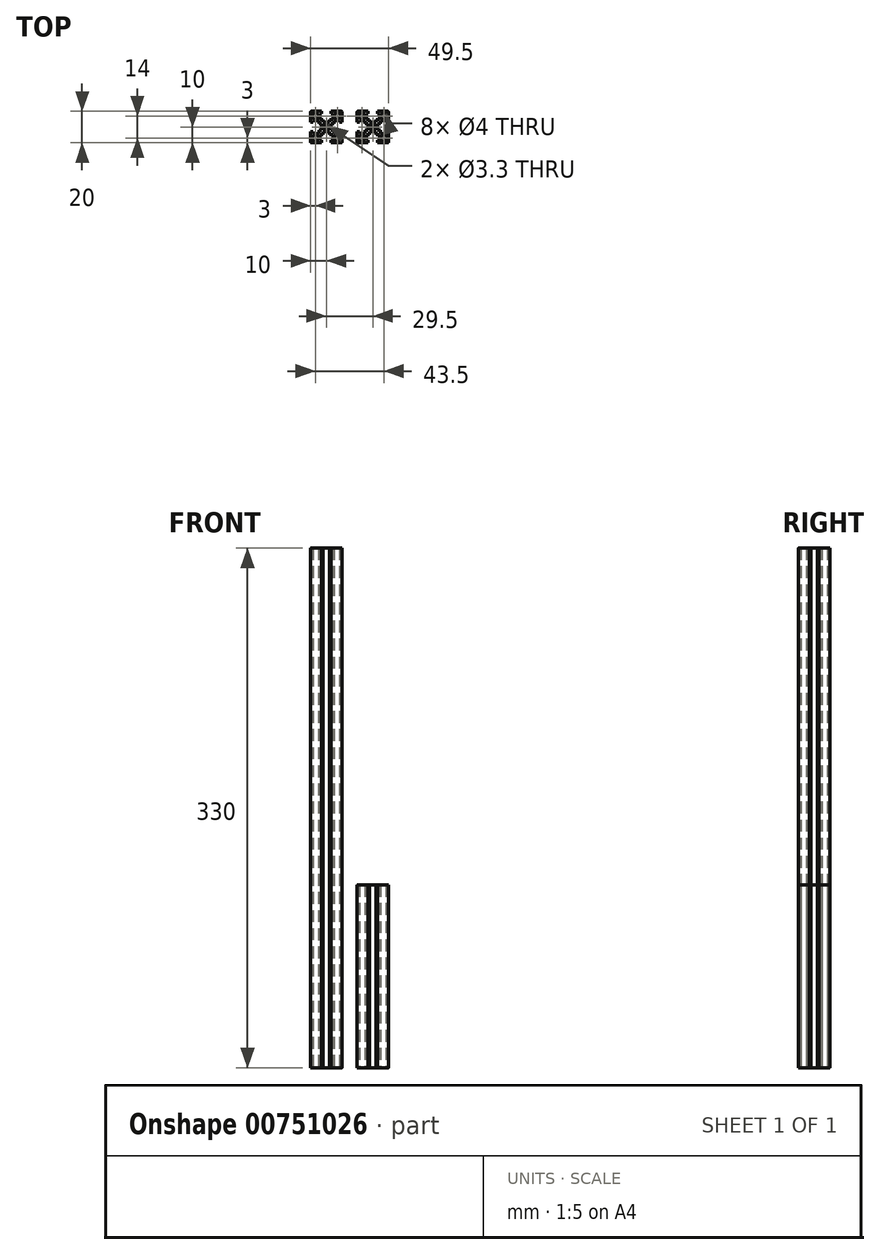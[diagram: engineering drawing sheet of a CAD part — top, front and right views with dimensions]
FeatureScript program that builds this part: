
annotation { "Feature Type Name" : "Feature", "Feature Type Description" : "" }
export const myFeature = defineFeature(function(context is Context, id is Id, definition is map)
    precondition{}
    {
        {
            var Q0;
            Q0=qCreatedBy(makeId("Top.planeOp"),FACE);
            var sketch = newSketch(context, id + "F0", { "sketchPlane" : qUnion([Q0])});
            skLineSegment(sketch, "E0", {"start": v(-9.48, 9.98) * mm, "end": v(-2.98, 9.98) * mm});
            skLineSegment(sketch, "E1", {"start": v(-2.98, 9.98) * mm, "end": v(-2.98, 8.48) * mm});
            skLineSegment(sketch, "E2", {"start": v(-2.98, 8.48) * mm, "end": v(-4.13, 8.48) * mm});
            skLineSegment(sketch, "E3", {"start": v(-4.13, 8.48) * mm, "end": v(-4.13, 4.78) * mm});
            skLineSegment(sketch, "E4", {"start": v(-4.13, 4.78) * mm, "end": v(-2.13, 4.78) * mm});
            skLineSegment(sketch, "E5", {"start": v(-2.13, 4.78) * mm, "end": v(-2.13, 2.98) * mm});
            skLineSegment(sketch, "E6", {"start": v(-2.13, 2.98) * mm, "end": v(0.02, 2.98) * mm});
            skLineSegment(sketch, "E7", {"start": v(0.02, 2.98) * mm, "end": v(0.02, -0.02) * mm});
            skLineSegment(sketch, "E8", {"start": v(0.02, -0.02) * mm, "end": v(-9.98, 9.98) * mm});
            skLineSegment(sketch, "E9.MirrorCS", {"start": v(-9.98, 9.48) * mm, "end": v(-9.98, 2.98) * mm});
            skLineSegment(sketch, "E10.MirrorCS", {"start": v(-8.48, 2.98) * mm, "end": v(-8.48, 4.13) * mm});
            skLineSegment(sketch, "E11.MirrorCS", {"start": v(-4.78, 2.13) * mm, "end": v(-2.98, 2.13) * mm});
            skLineSegment(sketch, "E12.MirrorCS", {"start": v(-9.98, 2.98) * mm, "end": v(-8.48, 2.98) * mm});
            skLineSegment(sketch, "E13.MirrorCS", {"start": v(-2.98, 2.13) * mm, "end": v(-2.98, -0.02) * mm});
            skLineSegment(sketch, "E14.MirrorCS", {"start": v(-4.78, 4.13) * mm, "end": v(-4.78, 2.13) * mm});
            skLineSegment(sketch, "E15.MirrorCS", {"start": v(-8.48, 4.13) * mm, "end": v(-4.78, 4.13) * mm});
            skLineSegment(sketch, "E16.MirrorCS", {"start": v(-2.98, -0.02) * mm, "end": v(0.02, -0.02) * mm});
            skCircle(sketch, "E17", {"center": v(-6.98, 6.98) * mm, "radius": 2 * mm});
            skLineSegment(sketch, "E18.1.0", {"start": v(-2.13, -3.02) * mm, "end": v(0.02, -3.02) * mm});
            skCircle(sketch, "E18.1.1", {"center": v(-6.98, -7.02) * mm, "radius": 2 * mm});
            skLineSegment(sketch, "E18.1.2", {"start": v(-2.98, -10.02) * mm, "end": v(-2.98, -8.52) * mm});
            skLineSegment(sketch, "E18.1.3", {"start": v(-2.13, -4.82) * mm, "end": v(-2.13, -3.02) * mm});
            skLineSegment(sketch, "E18.1.4", {"start": v(-2.98, -8.52) * mm, "end": v(-4.13, -8.52) * mm});
            skLineSegment(sketch, "E18.1.5", {"start": v(-9.48, -10.02) * mm, "end": v(-2.98, -10.02) * mm});
            skLineSegment(sketch, "E18.1.6", {"start": v(0.02, -0.02) * mm, "end": v(-9.98, -10.02) * mm});
            skLineSegment(sketch, "E18.1.7", {"start": v(-2.98, -2.17) * mm, "end": v(-2.98, -0.02) * mm});
            skLineSegment(sketch, "E18.1.8", {"start": v(-4.78, -2.17) * mm, "end": v(-2.98, -2.17) * mm});
            skLineSegment(sketch, "E18.1.9", {"start": v(-4.78, -4.17) * mm, "end": v(-4.78, -2.17) * mm});
            skLineSegment(sketch, "E18.1.10", {"start": v(-8.48, -4.17) * mm, "end": v(-4.78, -4.17) * mm});
            skLineSegment(sketch, "E18.1.11", {"start": v(-8.48, -3.02) * mm, "end": v(-8.48, -4.17) * mm});
            skLineSegment(sketch, "E18.1.12", {"start": v(-9.98, -3.02) * mm, "end": v(-8.48, -3.02) * mm});
            skLineSegment(sketch, "E18.1.13", {"start": v(-9.98, -9.52) * mm, "end": v(-9.98, -3.02) * mm});
            skLineSegment(sketch, "E18.1.14", {"start": v(-4.13, -8.52) * mm, "end": v(-4.13, -4.82) * mm});
            skLineSegment(sketch, "E18.1.15", {"start": v(-4.13, -4.82) * mm, "end": v(-2.13, -4.82) * mm});
            skLineSegment(sketch, "E18.2.0", {"start": v(3.02, -2.17) * mm, "end": v(3.02, -0.02) * mm});
            skCircle(sketch, "E18.2.1", {"center": v(7.02, -7.02) * mm, "radius": 2 * mm});
            skLineSegment(sketch, "E18.2.2", {"start": v(10.02, -3.02) * mm, "end": v(8.52, -3.02) * mm});
            skLineSegment(sketch, "E18.2.3", {"start": v(4.82, -2.17) * mm, "end": v(3.02, -2.17) * mm});
            skLineSegment(sketch, "E18.2.4", {"start": v(8.52, -3.02) * mm, "end": v(8.52, -4.17) * mm});
            skLineSegment(sketch, "E18.2.5", {"start": v(10.02, -9.52) * mm, "end": v(10.02, -3.02) * mm});
            skLineSegment(sketch, "E18.2.6", {"start": v(0.02, -0.02) * mm, "end": v(10.02, -10.02) * mm});
            skLineSegment(sketch, "E18.2.7", {"start": v(2.17, -3.02) * mm, "end": v(0.02, -3.02) * mm});
            skLineSegment(sketch, "E18.2.8", {"start": v(2.17, -4.82) * mm, "end": v(2.17, -3.02) * mm});
            skLineSegment(sketch, "E18.2.9", {"start": v(4.17, -4.82) * mm, "end": v(2.17, -4.82) * mm});
            skLineSegment(sketch, "E18.2.10", {"start": v(4.17, -8.52) * mm, "end": v(4.17, -4.82) * mm});
            skLineSegment(sketch, "E18.2.11", {"start": v(3.02, -8.52) * mm, "end": v(4.17, -8.52) * mm});
            skLineSegment(sketch, "E18.2.12", {"start": v(3.02, -10.02) * mm, "end": v(3.02, -8.52) * mm});
            skLineSegment(sketch, "E18.2.13", {"start": v(9.52, -10.02) * mm, "end": v(3.02, -10.02) * mm});
            skLineSegment(sketch, "E18.2.14", {"start": v(8.52, -4.17) * mm, "end": v(4.82, -4.17) * mm});
            skLineSegment(sketch, "E18.2.15", {"start": v(4.82, -4.17) * mm, "end": v(4.82, -2.17) * mm});
            skLineSegment(sketch, "E18.3.0", {"start": v(2.17, 2.98) * mm, "end": v(0.02, 2.98) * mm});
            skCircle(sketch, "E18.3.1", {"center": v(7.02, 6.98) * mm, "radius": 2 * mm});
            skLineSegment(sketch, "E18.3.2", {"start": v(3.02, 9.98) * mm, "end": v(3.02, 8.48) * mm});
            skLineSegment(sketch, "E18.3.3", {"start": v(2.17, 4.78) * mm, "end": v(2.17, 2.98) * mm});
            skLineSegment(sketch, "E18.3.4", {"start": v(3.02, 8.48) * mm, "end": v(4.17, 8.48) * mm});
            skLineSegment(sketch, "E18.3.5", {"start": v(9.52, 9.98) * mm, "end": v(3.02, 9.98) * mm});
            skLineSegment(sketch, "E18.3.6", {"start": v(0.02, -0.02) * mm, "end": v(10.02, 9.98) * mm});
            skLineSegment(sketch, "E18.3.7", {"start": v(3.02, 2.13) * mm, "end": v(3.02, -0.02) * mm});
            skLineSegment(sketch, "E18.3.8", {"start": v(4.82, 2.13) * mm, "end": v(3.02, 2.13) * mm});
            skLineSegment(sketch, "E18.3.9", {"start": v(4.82, 4.13) * mm, "end": v(4.82, 2.13) * mm});
            skLineSegment(sketch, "E18.3.10", {"start": v(8.52, 4.13) * mm, "end": v(4.82, 4.13) * mm});
            skLineSegment(sketch, "E18.3.11", {"start": v(8.52, 2.98) * mm, "end": v(8.52, 4.13) * mm});
            skLineSegment(sketch, "E18.3.12", {"start": v(10.02, 2.98) * mm, "end": v(8.52, 2.98) * mm});
            skLineSegment(sketch, "E18.3.13", {"start": v(10.02, 9.48) * mm, "end": v(10.02, 2.98) * mm});
            skLineSegment(sketch, "E18.3.14", {"start": v(4.17, 8.48) * mm, "end": v(4.17, 4.78) * mm});
            skLineSegment(sketch, "E18.3.15", {"start": v(4.17, 4.78) * mm, "end": v(2.17, 4.78) * mm});
            skPoint(sketch, "E18.center", {"position": v(0.02, -0.02) * mm});
            skCircle(sketch, "E19", {"center": v(0.02, -0.02) * mm, "radius": 1.65 * mm});
            skPoint(sketch, "E20.visualSharp", {"position": v(-9.98, 9.98) * mm});
            skArc(sketch, "E20.filletArc", {"start": v(-9.48, 9.98) * mm, "mid": v(-9.83, 9.83) * mm, "end": v(-9.98, 9.48) * mm});
            skPoint(sketch, "E21.visualSharp", {"position": v(10.02, 9.98) * mm});
            skArc(sketch, "E21.filletArc", {"start": v(10.02, 9.48) * mm, "mid": v(9.87, 9.83) * mm, "end": v(9.52, 9.98) * mm});
            skPoint(sketch, "E22.visualSharp", {"position": v(10.02, -10.02) * mm});
            skArc(sketch, "E22.filletArc", {"start": v(9.52, -10.02) * mm, "mid": v(9.87, -9.87) * mm, "end": v(10.02, -9.52) * mm});
            skPoint(sketch, "E23.visualSharp", {"position": v(-9.98, -10.02) * mm});
            skArc(sketch, "E23.filletArc", {"start": v(-9.98, -9.52) * mm, "mid": v(-9.83, -9.87) * mm, "end": v(-9.48, -10.02) * mm});
            skSolve(sketch);
        }
        {
            var Q0;
            {var subQ8=sQuery(id+"F0.wireOp",EDGE,"E0");Q0=makeQuery(id+"F0.imprint","IMPRINT",FACE,{"disambiguationData":[TD([[makeQuery(id+"F0.imprint","IMPRINT",EDGE,{"derivedFrom":subQ8}),-1.0]])]});}
            var Q1;
            {var subQ9=sQuery(id+"F0.wireOp",EDGE,"E18.3.0");Q1=makeQuery(id+"F0.imprint","IMPRINT",FACE,{"disambiguationData":[TD([[makeQuery(id+"F0.imprint","IMPRINT",EDGE,{"derivedFrom":subQ9}),1.0]])]});}
            var Q2;
            {var subQ0=sQuery(id+"F0.wireOp",EDGE,"E18.1.7");Q2=makeQuery(id+"F0.imprint","IMPRINT",FACE,{"disambiguationData":[TD([[makeQuery(id+"F0.imprint","IMPRINT",EDGE,{"derivedFrom":subQ0}),-1.0]])]});}
            var Q3;
            Q3=makeQuery(id+"F0.imprint","IMPRINT",FACE,{"disambiguationData":[TD([[makeQuery(id+"F0.imprint","IMPRINT",EDGE,{"derivedFrom":sQuery(id+"F0.wireOp",EDGE,"E18.2.0")}),1.0]])]});
            var Q4;
            {var subQ11=sQuery(id+"F0.wireOp",EDGE,"E9.MirrorCS");Q4=makeQuery(id+"F0.imprint","IMPRINT",FACE,{"disambiguationData":[TD([[makeQuery(id+"F0.imprint","IMPRINT",EDGE,{"derivedFrom":subQ11}),1.0]])]});}
            var Q5;
            Q5=makeQuery(id+"F0.imprint","IMPRINT",FACE,{"disambiguationData":[TD([[makeQuery(id+"F0.imprint","IMPRINT",EDGE,{"derivedFrom":sQuery(id+"F0.wireOp",EDGE,"E18.1.0")}),1.0]])]});
            extrude(context, id + "F1", {"entities" : qUnion([Q0, Q1, Q2, Q3, Q4, Q5]), "depth" : 330 * mm, "offsetDistance" : 25 * mm});
        }
        {
            var Q0;
            Q0=qCreatedBy(makeId("Top.planeOp"),FACE);
            var sketch = newSketch(context, id + "F2", { "sketchPlane" : qUnion([Q0])});
            skLineSegment(sketch, "E24", {"start": v(20.02, 9.98) * mm, "end": v(26.52, 9.98) * mm});
            skLineSegment(sketch, "E25", {"start": v(26.52, 9.98) * mm, "end": v(26.52, 8.48) * mm});
            skLineSegment(sketch, "E26", {"start": v(26.52, 8.48) * mm, "end": v(25.37, 8.48) * mm});
            skLineSegment(sketch, "E27", {"start": v(25.37, 8.48) * mm, "end": v(25.37, 4.78) * mm});
            skLineSegment(sketch, "E28", {"start": v(25.37, 4.78) * mm, "end": v(27.37, 4.78) * mm});
            skLineSegment(sketch, "E29", {"start": v(27.37, 4.78) * mm, "end": v(27.37, 2.98) * mm});
            skLineSegment(sketch, "E30", {"start": v(27.37, 2.98) * mm, "end": v(29.52, 2.98) * mm});
            skLineSegment(sketch, "E31", {"start": v(29.52, 2.98) * mm, "end": v(29.52, -0.02) * mm});
            skLineSegment(sketch, "E32", {"start": v(29.52, -0.02) * mm, "end": v(19.52, 9.98) * mm});
            skLineSegment(sketch, "E33.MirrorCS", {"start": v(19.52, 9.48) * mm, "end": v(19.52, 2.98) * mm});
            skLineSegment(sketch, "E34.MirrorCS", {"start": v(21.02, 2.98) * mm, "end": v(21.02, 4.13) * mm});
            skLineSegment(sketch, "E35.MirrorCS", {"start": v(24.72, 2.13) * mm, "end": v(26.52, 2.13) * mm});
            skLineSegment(sketch, "E36.MirrorCS", {"start": v(19.52, 2.98) * mm, "end": v(21.02, 2.98) * mm});
            skLineSegment(sketch, "E37.MirrorCS", {"start": v(26.52, 2.13) * mm, "end": v(26.52, -0.02) * mm});
            skLineSegment(sketch, "E38.MirrorCS", {"start": v(24.72, 4.13) * mm, "end": v(24.72, 2.13) * mm});
            skLineSegment(sketch, "E39.MirrorCS", {"start": v(21.02, 4.13) * mm, "end": v(24.72, 4.13) * mm});
            skLineSegment(sketch, "E40.MirrorCS", {"start": v(26.52, -0.02) * mm, "end": v(29.52, -0.02) * mm});
            skCircle(sketch, "E41", {"center": v(22.52, 6.98) * mm, "radius": 2 * mm});
            skLineSegment(sketch, "E42.1.0", {"start": v(27.37, -3.02) * mm, "end": v(29.52, -3.02) * mm});
            skCircle(sketch, "E42.1.1", {"center": v(22.52, -7.02) * mm, "radius": 2 * mm});
            skLineSegment(sketch, "E42.1.2", {"start": v(26.52, -10.02) * mm, "end": v(26.52, -8.52) * mm});
            skLineSegment(sketch, "E42.1.3", {"start": v(27.37, -4.82) * mm, "end": v(27.37, -3.02) * mm});
            skLineSegment(sketch, "E42.1.4", {"start": v(26.52, -8.52) * mm, "end": v(25.37, -8.52) * mm});
            skLineSegment(sketch, "E42.1.5", {"start": v(20.02, -10.02) * mm, "end": v(26.52, -10.02) * mm});
            skLineSegment(sketch, "E42.1.6", {"start": v(29.52, -0.02) * mm, "end": v(19.52, -10.02) * mm});
            skLineSegment(sketch, "E42.1.7", {"start": v(26.52, -2.17) * mm, "end": v(26.52, -0.02) * mm});
            skLineSegment(sketch, "E42.1.8", {"start": v(24.72, -2.17) * mm, "end": v(26.52, -2.17) * mm});
            skLineSegment(sketch, "E42.1.9", {"start": v(24.72, -4.17) * mm, "end": v(24.72, -2.17) * mm});
            skLineSegment(sketch, "E42.1.10", {"start": v(21.02, -4.17) * mm, "end": v(24.72, -4.17) * mm});
            skLineSegment(sketch, "E42.1.11", {"start": v(21.02, -3.02) * mm, "end": v(21.02, -4.17) * mm});
            skLineSegment(sketch, "E42.1.12", {"start": v(19.52, -3.02) * mm, "end": v(21.02, -3.02) * mm});
            skLineSegment(sketch, "E42.1.13", {"start": v(19.52, -9.52) * mm, "end": v(19.52, -3.02) * mm});
            skLineSegment(sketch, "E42.1.14", {"start": v(25.37, -8.52) * mm, "end": v(25.37, -4.82) * mm});
            skLineSegment(sketch, "E42.1.15", {"start": v(25.37, -4.82) * mm, "end": v(27.37, -4.82) * mm});
            skLineSegment(sketch, "E42.2.0", {"start": v(32.52, -2.17) * mm, "end": v(32.52, -0.02) * mm});
            skCircle(sketch, "E42.2.1", {"center": v(36.52, -7.02) * mm, "radius": 2 * mm});
            skLineSegment(sketch, "E42.2.2", {"start": v(39.52, -3.02) * mm, "end": v(38.02, -3.02) * mm});
            skLineSegment(sketch, "E42.2.3", {"start": v(34.32, -2.17) * mm, "end": v(32.52, -2.17) * mm});
            skLineSegment(sketch, "E42.2.4", {"start": v(38.02, -3.02) * mm, "end": v(38.02, -4.17) * mm});
            skLineSegment(sketch, "E42.2.5", {"start": v(39.52, -9.52) * mm, "end": v(39.52, -3.02) * mm});
            skLineSegment(sketch, "E42.2.6", {"start": v(29.52, -0.02) * mm, "end": v(39.52, -10.02) * mm});
            skLineSegment(sketch, "E42.2.7", {"start": v(31.67, -3.02) * mm, "end": v(29.52, -3.02) * mm});
            skLineSegment(sketch, "E42.2.8", {"start": v(31.67, -4.82) * mm, "end": v(31.67, -3.02) * mm});
            skLineSegment(sketch, "E42.2.9", {"start": v(33.67, -4.82) * mm, "end": v(31.67, -4.82) * mm});
            skLineSegment(sketch, "E42.2.10", {"start": v(33.67, -8.52) * mm, "end": v(33.67, -4.82) * mm});
            skLineSegment(sketch, "E42.2.11", {"start": v(32.52, -8.52) * mm, "end": v(33.67, -8.52) * mm});
            skLineSegment(sketch, "E42.2.12", {"start": v(32.52, -10.02) * mm, "end": v(32.52, -8.52) * mm});
            skLineSegment(sketch, "E42.2.13", {"start": v(39.02, -10.02) * mm, "end": v(32.52, -10.02) * mm});
            skLineSegment(sketch, "E42.2.14", {"start": v(38.02, -4.17) * mm, "end": v(34.32, -4.17) * mm});
            skLineSegment(sketch, "E42.2.15", {"start": v(34.32, -4.17) * mm, "end": v(34.32, -2.17) * mm});
            skLineSegment(sketch, "E42.3.0", {"start": v(31.67, 2.98) * mm, "end": v(29.52, 2.98) * mm});
            skCircle(sketch, "E42.3.1", {"center": v(36.52, 6.98) * mm, "radius": 2 * mm});
            skLineSegment(sketch, "E42.3.2", {"start": v(32.52, 9.98) * mm, "end": v(32.52, 8.48) * mm});
            skLineSegment(sketch, "E42.3.3", {"start": v(31.67, 4.78) * mm, "end": v(31.67, 2.98) * mm});
            skLineSegment(sketch, "E42.3.4", {"start": v(32.52, 8.48) * mm, "end": v(33.67, 8.48) * mm});
            skLineSegment(sketch, "E42.3.5", {"start": v(39.02, 9.98) * mm, "end": v(32.52, 9.98) * mm});
            skLineSegment(sketch, "E42.3.6", {"start": v(29.52, -0.02) * mm, "end": v(39.52, 9.98) * mm});
            skLineSegment(sketch, "E42.3.7", {"start": v(32.52, 2.13) * mm, "end": v(32.52, -0.02) * mm});
            skLineSegment(sketch, "E42.3.8", {"start": v(34.32, 2.13) * mm, "end": v(32.52, 2.13) * mm});
            skLineSegment(sketch, "E42.3.9", {"start": v(34.32, 4.13) * mm, "end": v(34.32, 2.13) * mm});
            skLineSegment(sketch, "E42.3.10", {"start": v(38.02, 4.13) * mm, "end": v(34.32, 4.13) * mm});
            skLineSegment(sketch, "E42.3.11", {"start": v(38.02, 2.98) * mm, "end": v(38.02, 4.13) * mm});
            skLineSegment(sketch, "E42.3.12", {"start": v(39.52, 2.98) * mm, "end": v(38.02, 2.98) * mm});
            skLineSegment(sketch, "E42.3.13", {"start": v(39.52, 9.48) * mm, "end": v(39.52, 2.98) * mm});
            skLineSegment(sketch, "E42.3.14", {"start": v(33.67, 8.48) * mm, "end": v(33.67, 4.78) * mm});
            skLineSegment(sketch, "E42.3.15", {"start": v(33.67, 4.78) * mm, "end": v(31.67, 4.78) * mm});
            skPoint(sketch, "E42.center", {"position": v(29.52, -0.02) * mm});
            skCircle(sketch, "E43", {"center": v(29.52, -0.02) * mm, "radius": 1.65 * mm});
            skPoint(sketch, "E44.visualSharp", {"position": v(19.52, 9.98) * mm});
            skArc(sketch, "E44.filletArc", {"start": v(20.02, 9.98) * mm, "mid": v(19.67, 9.83) * mm, "end": v(19.52, 9.48) * mm});
            skPoint(sketch, "E45.visualSharp", {"position": v(39.52, 9.98) * mm});
            skArc(sketch, "E45.filletArc", {"start": v(39.52, 9.48) * mm, "mid": v(39.37, 9.83) * mm, "end": v(39.02, 9.98) * mm});
            skPoint(sketch, "E46.visualSharp", {"position": v(39.52, -10.02) * mm});
            skArc(sketch, "E46.filletArc", {"start": v(39.02, -10.02) * mm, "mid": v(39.37, -9.87) * mm, "end": v(39.52, -9.52) * mm});
            skPoint(sketch, "E47.visualSharp", {"position": v(19.52, -10.02) * mm});
            skArc(sketch, "E47.filletArc", {"start": v(19.52, -9.52) * mm, "mid": v(19.67, -9.87) * mm, "end": v(20.02, -10.02) * mm});
            skSolve(sketch);
        }
        {
            var Q0;
            Q0=makeQuery(id+"F2.imprint","IMPRINT",FACE,{"disambiguationData":[TD([[makeQuery(id+"F2.imprint","IMPRINT",EDGE,{"derivedFrom":sQuery(id+"F2.wireOp",EDGE,"E42.1.0")}),1.0]])]});
            var Q1;
            {var subQ11=sQuery(id+"F2.wireOp",EDGE,"E33.MirrorCS");Q1=makeQuery(id+"F2.imprint","IMPRINT",FACE,{"disambiguationData":[TD([[makeQuery(id+"F2.imprint","IMPRINT",EDGE,{"derivedFrom":subQ11}),1.0]])]});}
            var Q2;
            {var subQ8=sQuery(id+"F2.wireOp",EDGE,"E24");Q2=makeQuery(id+"F2.imprint","IMPRINT",FACE,{"disambiguationData":[TD([[makeQuery(id+"F2.imprint","IMPRINT",EDGE,{"derivedFrom":subQ8}),-1.0]])]});}
            var Q3;
            Q3=makeQuery(id+"F2.imprint","IMPRINT",FACE,{"disambiguationData":[TD([[makeQuery(id+"F2.imprint","IMPRINT",EDGE,{"derivedFrom":sQuery(id+"F2.wireOp",EDGE,"E42.2.0")}),1.0]])]});
            var Q4;
            {var subQ0=sQuery(id+"F2.wireOp",EDGE,"E42.1.7");Q4=makeQuery(id+"F2.imprint","IMPRINT",FACE,{"disambiguationData":[TD([[makeQuery(id+"F2.imprint","IMPRINT",EDGE,{"derivedFrom":subQ0}),-1.0]])]});}
            var Q5;
            {var subQ9=sQuery(id+"F2.wireOp",EDGE,"E42.3.0");Q5=makeQuery(id+"F2.imprint","IMPRINT",FACE,{"disambiguationData":[TD([[makeQuery(id+"F2.imprint","IMPRINT",EDGE,{"derivedFrom":subQ9}),1.0]])]});}
            extrude(context, id + "F3", {"entities" : qUnion([Q0, Q1, Q2, Q3, Q4, Q5]), "depth" : 116 * mm, "offsetDistance" : 25 * mm});
        }
    });
